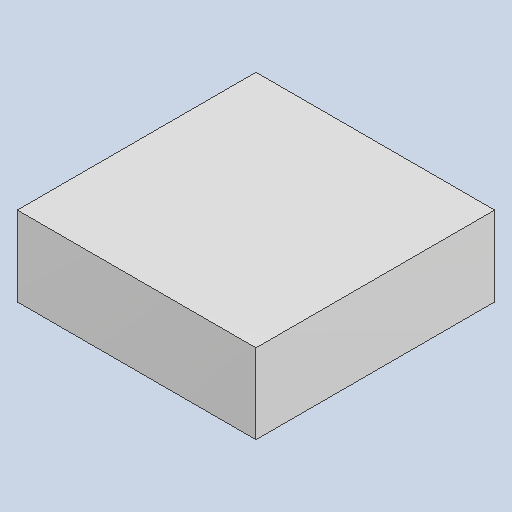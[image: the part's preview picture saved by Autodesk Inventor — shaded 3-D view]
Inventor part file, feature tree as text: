
AUTODESK INVENTOR PART (.ipt)
format: ipt  version: 2023.4 (Build 274418000, 418)  size: 79,872 bytes
history: native  units: mm
features: extrude x1
ambient origin geometry x8: Origin, YZ Plane, XZ Plane, XY Plane, X Axis, Y Axis, Z Axis, Center Point
bodies: Solid1 (feature_tree)
feature tree (1):
  extrude  "Extruded_45"  [1 undecoded]
note: 1 required parameter value undecoded (feature->parameter linkage not recoverable at this tier; creation-order binding heuristic only, values carry confidence <= 0.55)
